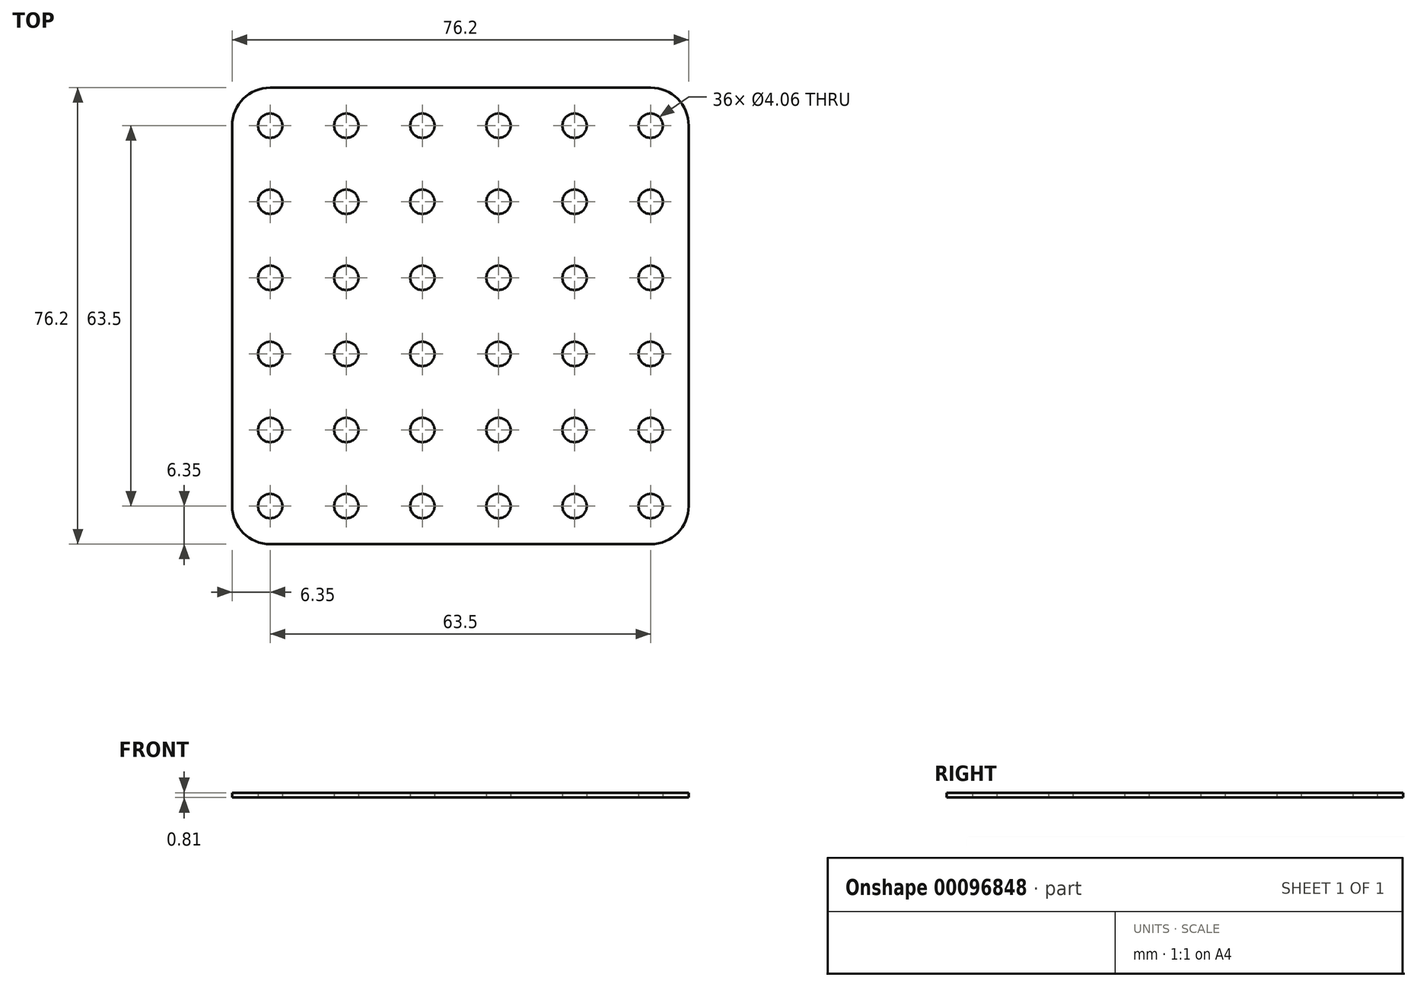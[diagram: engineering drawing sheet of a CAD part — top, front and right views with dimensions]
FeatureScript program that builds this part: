
annotation { "Feature Type Name" : "Feature", "Feature Type Description" : "" }
export const myFeature = defineFeature(function(context is Context, id is Id, definition is map)
    precondition{}
    {
        {
            var Q0;
            Q0=qCreatedBy(makeId("Top.planeOp"),FACE);
            var sketch = newSketch(context, id + "F0", { "sketchPlane" : qUnion([Q0])});
            skLineSegment(sketch, "E0.bottom", {"start": v(-38.1, 38.1) * mm, "end": v(38.1, 38.1) * mm});
            skLineSegment(sketch, "E0.top", {"start": v(-38.1, -38.1) * mm, "end": v(38.1, -38.1) * mm});
            skLineSegment(sketch, "E0.left", {"start": v(-38.1, 38.1) * mm, "end": v(-38.1, -38.1) * mm});
            skLineSegment(sketch, "E0.right", {"start": v(38.1, 38.1) * mm, "end": v(38.1, -38.1) * mm});
            skPoint(sketch, "E0.middle", {"position": v(0, 0) * mm});
            skLineSegment(sketch, "E1.top", {"start": v(-31.75, -31.75) * mm, "end": v(31.75, -31.75) * mm, "construction": true});
            skLineSegment(sketch, "E1.right", {"start": v(31.75, 31.75) * mm, "end": v(31.75, -31.75) * mm, "construction": true});
            skLineSegment(sketch, "E2", {"start": v(-31.75, 31.75) * mm, "end": v(-19.05, 31.75) * mm, "construction": true});
            skLineSegment(sketch, "E3", {"start": v(-19.05, 31.75) * mm, "end": v(-6.35, 31.75) * mm, "construction": true});
            skLineSegment(sketch, "E4", {"start": v(-6.35, 31.75) * mm, "end": v(6.35, 31.75) * mm, "construction": true});
            skLineSegment(sketch, "E5", {"start": v(6.35, 31.75) * mm, "end": v(19.05, 31.75) * mm, "construction": true});
            skLineSegment(sketch, "E6", {"start": v(19.05, 31.75) * mm, "end": v(31.75, 31.75) * mm, "construction": true});
            skLineSegment(sketch, "E7", {"start": v(19.05, 31.75) * mm, "end": v(19.05, -31.75) * mm, "construction": true});
            skLineSegment(sketch, "E8", {"start": v(6.35, 31.75) * mm, "end": v(6.35, -31.75) * mm, "construction": true});
            skLineSegment(sketch, "E9", {"start": v(-6.35, 31.75) * mm, "end": v(-6.35, -31.75) * mm, "construction": true});
            skLineSegment(sketch, "E10", {"start": v(-19.05, 31.75) * mm, "end": v(-19.05, -31.75) * mm, "construction": true});
            skLineSegment(sketch, "E11", {"start": v(-31.75, 31.75) * mm, "end": v(-31.75, 19.05) * mm, "construction": true});
            skLineSegment(sketch, "E12", {"start": v(-31.75, 19.05) * mm, "end": v(-31.75, 6.35) * mm, "construction": true});
            skLineSegment(sketch, "E13", {"start": v(-31.75, 6.35) * mm, "end": v(-31.75, -6.35) * mm, "construction": true});
            skLineSegment(sketch, "E14", {"start": v(-31.75, -6.35) * mm, "end": v(-31.75, -19.05) * mm, "construction": true});
            skLineSegment(sketch, "E15", {"start": v(-31.75, -19.05) * mm, "end": v(-31.75, -31.75) * mm, "construction": true});
            skLineSegment(sketch, "E16", {"start": v(-31.75, 19.05) * mm, "end": v(31.75, 19.05) * mm, "construction": true});
            skLineSegment(sketch, "E17", {"start": v(-31.75, 6.35) * mm, "end": v(31.75, 6.35) * mm, "construction": true});
            skLineSegment(sketch, "E18", {"start": v(-31.75, -6.35) * mm, "end": v(31.75, -6.35) * mm, "construction": true});
            skLineSegment(sketch, "E19", {"start": v(-31.75, -19.05) * mm, "end": v(31.75, -19.05) * mm, "construction": true});
            skCircle(sketch, "E20", {"center": v(-31.75, 31.75) * mm, "radius": 2.03 * mm});
            skCircle(sketch, "E21.1.0.0", {"center": v(-19.05, 31.75) * mm, "radius": 2.03 * mm});
            skCircle(sketch, "E21.2.0.0", {"center": v(-6.35, 31.75) * mm, "radius": 2.03 * mm});
            skCircle(sketch, "E22.0.3.0", {"center": v(6.35, 31.75) * mm, "radius": 2.03 * mm});
            skCircle(sketch, "E22.0.4.0", {"center": v(19.05, 31.75) * mm, "radius": 2.03 * mm});
            skCircle(sketch, "E22.0.5.0", {"center": v(31.75, 31.75) * mm, "radius": 2.03 * mm});
            skCircle(sketch, "E23.1.0.0", {"center": v(-31.75, 19.05) * mm, "radius": 2.03 * mm});
            skCircle(sketch, "E23.1.0.1", {"center": v(-19.05, 19.05) * mm, "radius": 2.03 * mm});
            skCircle(sketch, "E23.1.0.2", {"center": v(-6.35, 19.05) * mm, "radius": 2.03 * mm});
            skCircle(sketch, "E23.1.0.3", {"center": v(6.35, 19.05) * mm, "radius": 2.03 * mm});
            skCircle(sketch, "E23.1.0.4", {"center": v(19.05, 19.05) * mm, "radius": 2.03 * mm});
            skCircle(sketch, "E23.1.0.5", {"center": v(31.75, 19.05) * mm, "radius": 2.03 * mm});
            skCircle(sketch, "E23.2.0.0", {"center": v(-31.75, 6.35) * mm, "radius": 2.03 * mm});
            skCircle(sketch, "E23.2.0.1", {"center": v(-19.05, 6.35) * mm, "radius": 2.03 * mm});
            skCircle(sketch, "E23.2.0.2", {"center": v(-6.35, 6.35) * mm, "radius": 2.03 * mm});
            skCircle(sketch, "E23.2.0.3", {"center": v(6.35, 6.35) * mm, "radius": 2.03 * mm});
            skCircle(sketch, "E23.2.0.4", {"center": v(19.05, 6.35) * mm, "radius": 2.03 * mm});
            skCircle(sketch, "E23.2.0.5", {"center": v(31.75, 6.35) * mm, "radius": 2.03 * mm});
            skCircle(sketch, "E24.0.3.0", {"center": v(-31.75, -6.35) * mm, "radius": 2.03 * mm});
            skCircle(sketch, "E24.2.3.0", {"center": v(-19.05, -6.35) * mm, "radius": 2.03 * mm});
            skCircle(sketch, "E24.4.3.0", {"center": v(-6.35, -6.35) * mm, "radius": 2.03 * mm});
            skCircle(sketch, "E24.6.3.0", {"center": v(6.35, -6.35) * mm, "radius": 2.03 * mm});
            skCircle(sketch, "E24.8.3.0", {"center": v(19.05, -6.35) * mm, "radius": 2.03 * mm});
            skCircle(sketch, "E24.10.3.0", {"center": v(31.75, -6.35) * mm, "radius": 2.03 * mm});
            skCircle(sketch, "E24.0.4.0", {"center": v(-31.75, -19.05) * mm, "radius": 2.03 * mm});
            skCircle(sketch, "E24.2.4.0", {"center": v(-19.05, -19.05) * mm, "radius": 2.03 * mm});
            skCircle(sketch, "E24.4.4.0", {"center": v(-6.35, -19.05) * mm, "radius": 2.03 * mm});
            skCircle(sketch, "E24.6.4.0", {"center": v(6.35, -19.05) * mm, "radius": 2.03 * mm});
            skCircle(sketch, "E24.8.4.0", {"center": v(19.05, -19.05) * mm, "radius": 2.03 * mm});
            skCircle(sketch, "E24.10.4.0", {"center": v(31.75, -19.05) * mm, "radius": 2.03 * mm});
            skCircle(sketch, "E24.0.5.0", {"center": v(-31.75, -31.75) * mm, "radius": 2.03 * mm});
            skCircle(sketch, "E24.2.5.0", {"center": v(-19.05, -31.75) * mm, "radius": 2.03 * mm});
            skCircle(sketch, "E24.4.5.0", {"center": v(-6.35, -31.75) * mm, "radius": 2.03 * mm});
            skCircle(sketch, "E24.6.5.0", {"center": v(6.35, -31.75) * mm, "radius": 2.03 * mm});
            skCircle(sketch, "E24.8.5.0", {"center": v(19.05, -31.75) * mm, "radius": 2.03 * mm});
            skCircle(sketch, "E24.10.5.0", {"center": v(31.75, -31.75) * mm, "radius": 2.03 * mm});
            skSolve(sketch);
        }
        {
            var Q0;
            Q0=makeQuery(id+"F0.imprint","IMPRINT",FACE,{"disambiguationData":[TD([[makeQuery(id+"F0.imprint","IMPRINT",EDGE,{"derivedFrom":sQuery(id+"F0.wireOp",EDGE,"E0.bottom")}),-1.0]])]});
            extrude(context, id + "F1", {"entities" : qUnion([Q0]), "depth" : 0.81 * mm});
        }
        {
            var Q0;
            Q0=makeQuery(id+"F1.opExtrude","SWEPT_EDGE",EDGE,{"disambiguationData":[OSD([sQuery(id+"F0.wireOp",EDGE,"E0.top"),sQuery(id+"F0.wireOp",EDGE,"E0.left")])]});
            var Q1;
            Q1=makeQuery(id+"F1.opExtrude","SWEPT_EDGE",EDGE,{"disambiguationData":[OSD([sQuery(id+"F0.wireOp",EDGE,"E0.top"),sQuery(id+"F0.wireOp",EDGE,"E0.right")])]});
            var Q2;
            Q2=makeQuery(id+"F1.opExtrude","SWEPT_EDGE",EDGE,{"disambiguationData":[OSD([sQuery(id+"F0.wireOp",EDGE,"E0.bottom"),sQuery(id+"F0.wireOp",EDGE,"E0.right")])]});
            var Q3;
            Q3=makeQuery(id+"F1.opExtrude","SWEPT_EDGE",EDGE,{"disambiguationData":[OSD([sQuery(id+"F0.wireOp",EDGE,"E0.bottom"),sQuery(id+"F0.wireOp",EDGE,"E0.left")])]});
            fillet(context, id + "F2", {"entities" : qUnion([Q0, Q1, Q2, Q3]), "radius" : 6.35 * mm, "tangentPropagation" : true, "allowEdgeOverflow" : false});
        }
    });
